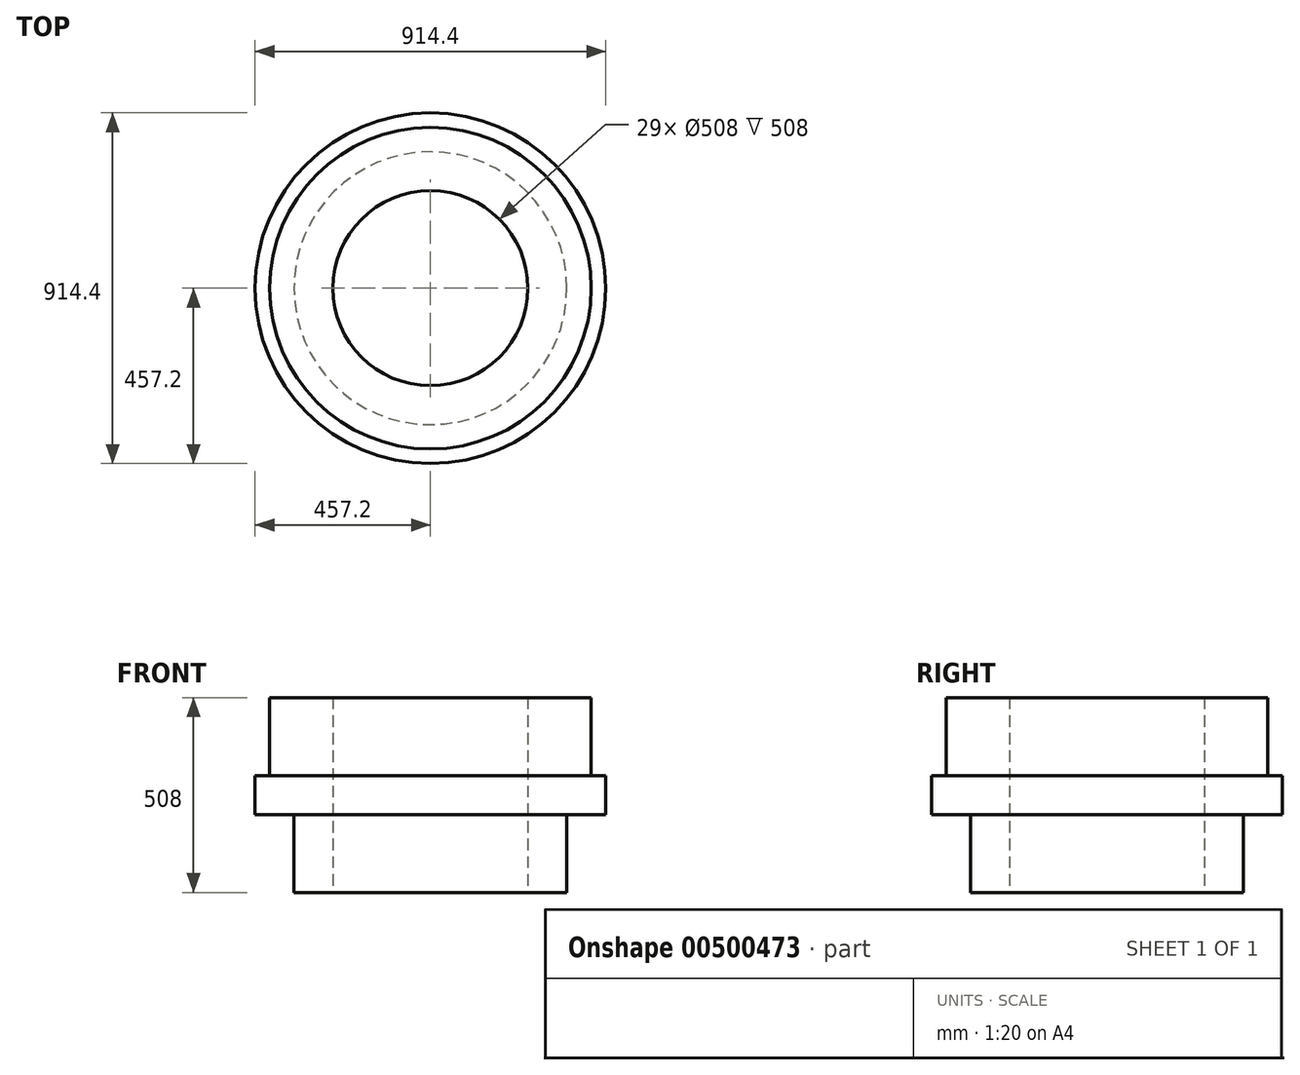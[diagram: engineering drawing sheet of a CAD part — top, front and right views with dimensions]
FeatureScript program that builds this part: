
annotation { "Feature Type Name" : "Feature", "Feature Type Description" : "" }
export const myFeature = defineFeature(function(context is Context, id is Id, definition is map)
    precondition{}
    {
        {
            var Q0;
            Q0=qCreatedBy(makeId("Top.planeOp"),FACE);
            var sketch = newSketch(context, id + "F0", { "sketchPlane" : qUnion([Q0])});
            skCircle(sketch, "E0", {"center": v(0, 0) * mm, "radius": 457.2 * mm});
            skCircle(sketch, "E1", {"center": v(0, 0) * mm, "radius": 254 * mm});
            skSolve(sketch);
        }
        {
            var Q0;
            Q0=makeQuery(id+"F0.imprint","IMPRINT",FACE,{"disambiguationData":[TD([[makeQuery(id+"F0.imprint","IMPRINT",EDGE,{"derivedFrom":sQuery(id+"F0.wireOp",EDGE,"E0")}),1.0]])]});
            extrude(context, id + "F1", {"entities" : qUnion([Q0]), "depth" : 508 * mm});
        }
        {
            var Q0;
            Q0=makeQuery(id+"F1.opExtrude","CAP_FACE",FACE,{"disambiguationData":[OSD([sQuery(id+"F0.wireOp",EDGE,"E0"),sQuery(id+"F0.wireOp",EDGE,"E1")])],"isStart":false});
            var sketch = newSketch(context, id + "F2", { "sketchPlane" : qUnion([Q0])});
            skCircle(sketch, "E2", {"center": v(0, 0) * mm, "radius": 419.1 * mm});
            skSolve(sketch);
        }
        {
            var Q0;
            Q0=makeQuery(id+"F2.imprint","IMPRINT",FACE,{"disambiguationData":[TD([[makeQuery(id+"F2.imprint","IMPRINT",EDGE,{"derivedFrom":sQuery(id+"F2.wireOp",EDGE,"E2")}),-1.0]])]});
            extrude(context, id + "F3", {"entities" : qUnion([Q0]), "operationType" : NewBodyOperationType.REMOVE, "oppositeDirection" : true, "depth" : 203.2 * mm});
        }
        {
            var Q0;
            Q0=makeQuery(id+"F0.imprint","IMPRINT",FACE,{"disambiguationData":[TD([[makeQuery(id+"F0.imprint","IMPRINT",EDGE,{"derivedFrom":sQuery(id+"F0.wireOp",EDGE,"E0")}),1.0]])]});
            var sketch = newSketch(context, id + "F4", { "sketchPlane" : qUnion([Q0])});
            skCircle(sketch, "E3", {"center": v(0, 0) * mm, "radius": 355.6 * mm});
            skSolve(sketch);
        }
        {
            var Q0;
            Q0=makeQuery(id+"F4.imprint","IMPRINT",FACE,{"disambiguationData":[TD([[makeQuery(id+"F4.imprint","IMPRINT",EDGE,{"derivedFrom":sQuery(id+"F4.wireOp",EDGE,"E3")}),-1.0]])]});
            extrude(context, id + "F5", {"entities" : qUnion([Q0]), "operationType" : NewBodyOperationType.REMOVE, "depth" : 203.2 * mm});
        }
    });
